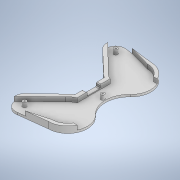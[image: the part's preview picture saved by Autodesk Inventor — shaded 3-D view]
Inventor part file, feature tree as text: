
AUTODESK INVENTOR PART (.ipt)
format: ipt  version: 2021 (Build 250183000, 183)  size: 269,312 bytes
history: native  units: mm
features: extrude x5, sketch x5, fillet x2, other x1
ambient origin geometry x8: Origin, YZ Plane, XZ Plane, XY Plane, X Axis, Y Axis, Z Axis, Center Point
bodies: Body1 (feature_tree)
feature tree (13):
  other  "Sólido1"
  extrude  "Extrusión1"  Depth=75.0mm
  extrude  "Extrusión2"  Depth=9.0mm
  extrude  "Extrusión3"  Depth=10.0mm
  fillet  "Empalme1"  Radius=10.0mm
  extrude  "Extrusión4"  Depth=15.0mm
  fillet  "Empalme2"  Radius=15.0mm
  extrude  "Extrusión5"  Depth=15.0mm TaperAngle=0.0deg
  sketch  "Boceto1"  dims[d3=75.0mm d4=75.0mm]
  sketch  "Boceto2"  dims[d7=135.0mm d8=9.0mm]
  sketch  "Boceto3"  dims[d9=9.0mm d10=9.0mm d11=10.0mm d12=0.0mm]
  sketch  "Boceto4"  dims[d13=5.0mm d14=0.0mm d15=15.0mm d16=15.0mm]
  sketch  "Boceto5"  dims[d17=8.0mm d18=15.0mm d19=0.0mm d20=2.0mm d21=8.0mm d22=0.0mm d23=2.0mm d24=30.0mm d25=0.0mm]
